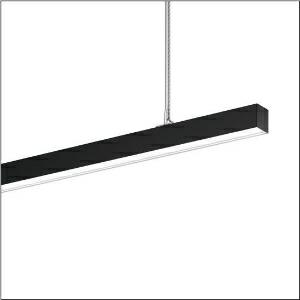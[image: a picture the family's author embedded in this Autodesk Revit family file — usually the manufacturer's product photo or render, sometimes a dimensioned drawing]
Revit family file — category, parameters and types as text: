
# Revit family: silica_r__21_51mx33db39bb_fd0d
name_source: partatom
category: Lighting Fixtures
units: mm (PartAtom-declared; Revit-internal decimal feet)

## family parameters
Cut with Voids When Loaded = No
Host = Face
Light Source = No
Part Type = Normal
Room Calculation Point = No
Round Connector Dimension = Use Diameter
Shared = No

## types (1)
- --- (1 x LED, 7390 lm, 51.6 W, 3000K)
    Apparent Load = 52 VA
    CIE Flux Codes = 78 96 99 55 100
    Color Rendering = 80
    Color Temperature = 3000K
    Default Elevation = 1800 mm
    Description = Silica® 21, office luminaire, primary optical cover: prismatic diffuser, of PMMA, CAT 2 (L<= 3000cd/m²), light emission: direct/indirect distribution, primary light characteristic: symmetric, installation type: suspended mounting, LED, rated luminous flux: 7.390lm, luminous efficacy: 143lm/W, light colour: 830, colour temperature: 3000K, control gear: DALI 2, with terminal, 3+2-pole, max. 2.5mm², mains connection: 220..240V, AC, 50/60Hz, rated input power: 51.6W, luminaire housing, of aluminium, matt jet black (RAL 9005), length: 1.504mm, width: 53mm, height: 53mm, protection rating (complete): IP20, insulation class (complete): insulation class I (protective earthing), certification: CE, permissible operating ambient temperature: 0..+35°C, standard: EN 50419, packaging unit: 1 piece
    Height = 53 mm
    Lamp = 1 x LED
    Lamp Light Flux = 7390 lm
    Lamp Power = 51.6 W
    Lamp count = 1
    Length = 1504 mm
    Luminous efficacy = 143 lm/W
    Manufacturer = Siteco
    ModVariant = No
    Model = 51MX33DB39BB
    Mounting Place = Ceiling
    Mounting Type = Pendant
    Number of Poles = 1
    OnlyDefault = Yes
    Power Factor = 1
    Product Name = Silica® 21
    Product group = office luminaire | ceiling pendant
    ProductGroupID = 904
    Protection Class = Protection class I
    Protection Degree = IP 20
    RLX_Detail_Level = 1
    RLX_Emergency_Light_Flux = 0 lm
    RLX_Emergency_Type = 0
    RLX_Emergency_Type_DB = No
    RlxData = <blob elided: 26281 chars, md5=be61dcfd>
    Socket = socket
    Standby Power = 0 W
    System Light Flux = 7390 lm
    System Power = 52 W
    Type Comments = factory setting: luminous flux: 100 % | dim-lin: 254 | 345 mA
    Type Image = l_1335856.jpg
    URL = http://relux.com
    VarID = @adj_118378
    Voltage = 0 V
    Weight = 0.00 kg
    Width = 53 mm

## geometry (parser evidence)
native form markers: Blend x4, Sweep x12
no freeform markers — native parametric forms only
